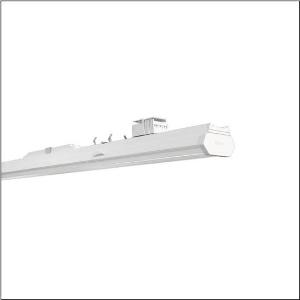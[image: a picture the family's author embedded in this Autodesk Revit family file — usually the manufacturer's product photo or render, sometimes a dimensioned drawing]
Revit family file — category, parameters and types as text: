
# Revit family: licross_11_protected_ho_51td13mn4gxs
name_source: partatom
category: Lighting Fixtures
units: mm (PartAtom-declared; Revit-internal decimal feet)

## family parameters
Cut with Voids When Loaded = No
Host = Face
Light Source = No
Part Type = Normal
Room Calculation Point = No
Round Connector Dimension = Use Diameter
Shared = No

## types (1)
- --- (1 x LED, 16110 lm, 87.4 W, 4000K)
    Apparent Load = 87 VA
    CIE Flux Codes = 89 96 99 100 99
    Color Rendering = 80
    Color Temperature = 4000K
    Default Elevation = 1800 mm
    Description = Licross 11 Protected HO, luminaire insert, of sheet steel, galvanised, coil coated, white, length: 1.500mm, width: 90mm, height: 101mm, LED rated luminous flux: 16.110lm, light colour: 840, SDCM (Standard Deviation of Colour Matching)MacAdam ≤ 2 SDCM (initial), control gear: ON/OFF Multilumen, with plug, 3-pole, with phase selection, mains connection: 220..240V, AC, 50/60Hz, rated input power: 87W, internal wiring halogen-free, primary light control with lens, of plastic, primary optical cover: cover, of PMMA, light emission: direct distribution, primary light characteristic: symmetric, protection rating (complete): IP54, insulation class (complete): insulation class I (protective earthing), certification: CE, ENEC, VDE, UKCA, protection symbol: D if used in an environment with non-conductive dust loads with corresponding accessories, impact resistance: IK06, permissible ambient temperature for indoor applications: -35..+35°C, corresponds to IFS (International Featured Standards) requirements for safety and quality in the food industry, reducing of maximum allowable ambient temperature of 5°C with ceiling mounting, LABS conformity tested according to VDMA 24364:2018-05, The light source and the operating device comply with the requirements of the Ecodesign Regulation (EU) 2019/2020 and are replaceable in accordance with this regulation, packaging unit: 1 piece
    Height = 92 mm
    Lamp = 1 x LED
    Lamp Light Flux = 16110 lm
    Lamp Power = 87.4 W
    Lamp count = 1
    Length = 1500 mm
    Luminous efficacy = 184 lm/W
    Manufacturer = Siteco
    ModVariant = No
    Model = 51TD13MN4GXS
    Mounting Place = Ceiling
    Mounting Type = Pendant
    Number of Poles = 1
    OnlyDefault = Yes
    Power Factor = 1
    Product Name = Licross 11 Protected HO
    Product group = luminaire insert | ceiling pendant
    ProductGroupID = 901
    Protection Class = Protection class I
    Protection Degree = IP 54
    RLX_Detail_Level = 1
    RLX_Emergency_Light_Flux = 0 lm
    RLX_Emergency_Type = 0
    RLX_Emergency_Type_DB = No
    RlxData = <blob elided: 22281 chars, md5=0ce352ad>
    Socket = socket
    Standby Power = 0 W
    System Light Flux = 16110 lm
    System Power = 87 W
    Type Comments = factory setting: luminous flux: 100 % | (A | C | E) | 203 mA
    Type Image = l_1256145.jpg
    URL = http://relux.com
    VarID = @adj_091925
    Voltage = 0 V
    Weight = 0.00 kg
    Width = 88 mm

## geometry (parser evidence)
native form markers: Blend x4, Sweep x13
no freeform markers — native parametric forms only
